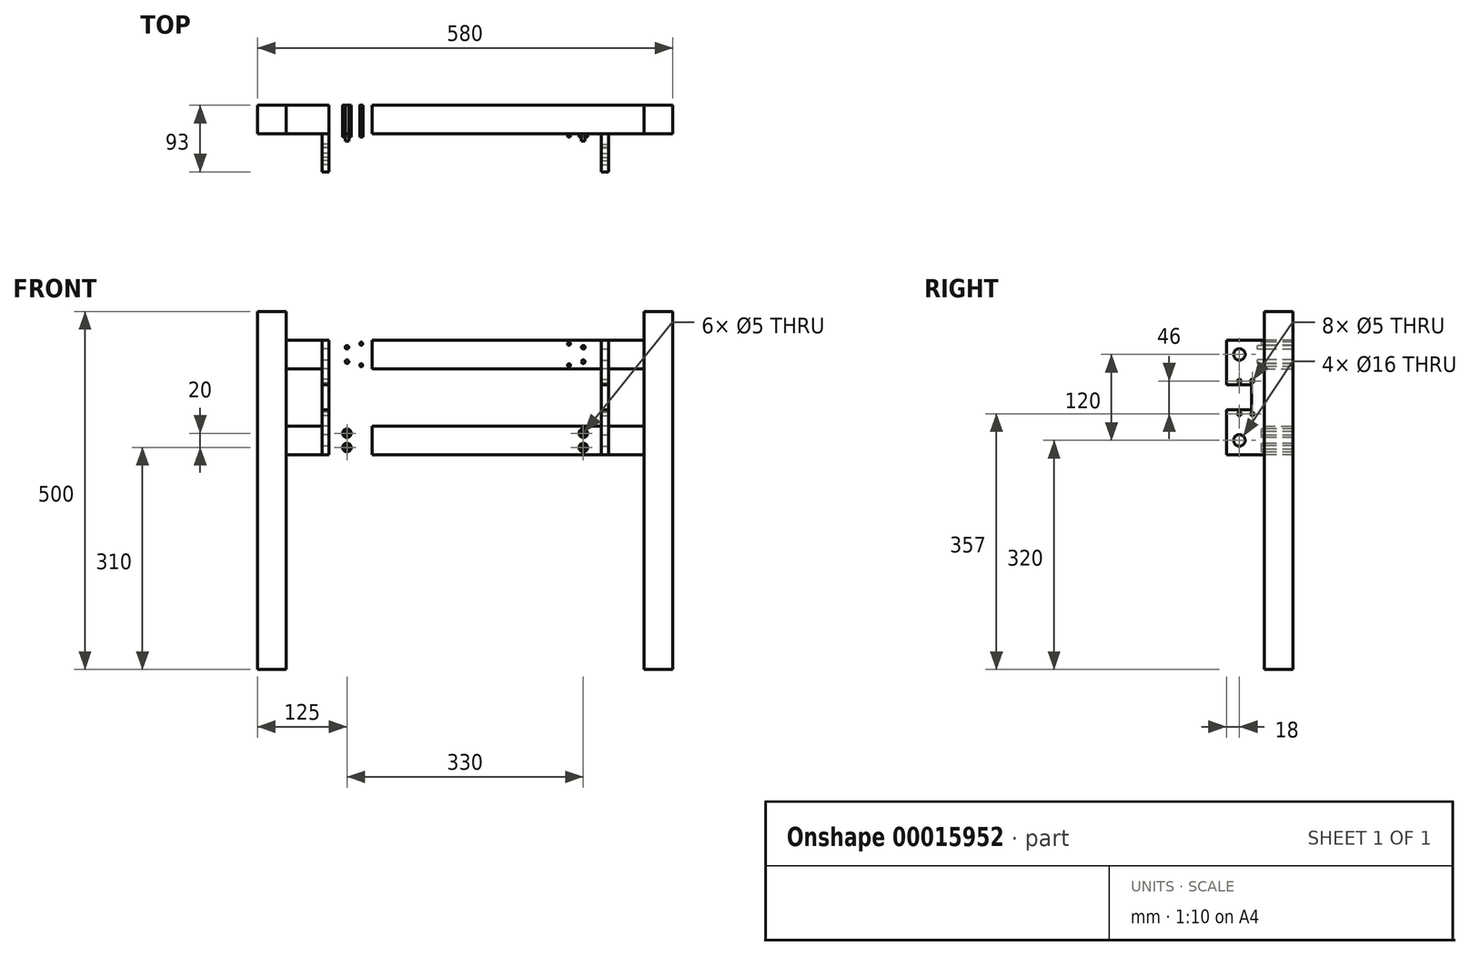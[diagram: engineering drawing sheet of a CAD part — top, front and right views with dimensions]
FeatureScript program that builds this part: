
annotation { "Feature Type Name" : "Feature", "Feature Type Description" : "" }
export const myFeature = defineFeature(function(context is Context, id is Id, definition is map)
    precondition{}
    {
        {
            var Q0;
            Q0=qCreatedBy(makeId("Top.planeOp"),FACE);
            var sketch = newSketch(context, id + "F0", { "sketchPlane" : qUnion([Q0])});
            skLineSegment(sketch, "E0.bottom", {"start": v(0, 0) * mm, "end": v(40, 0) * mm});
            skLineSegment(sketch, "E0.top", {"start": v(0, 40) * mm, "end": v(40, 40) * mm});
            skLineSegment(sketch, "E0.left", {"start": v(0, 0) * mm, "end": v(0, 40) * mm});
            skLineSegment(sketch, "E0.right", {"start": v(40, 0) * mm, "end": v(40, 40) * mm});
            skSolve(sketch);
        }
        {
            var Q0;
            Q0 = qSketchRegion(id + "F0", true);
            extrude(context, id + "F1", {"entities" : qUnion([Q0]), "depth" : 500 * mm});
        }
        {
            var Q0;
            Q0=makeQuery(id+"F1.opExtrude","SWEPT_FACE",FACE,{"disambiguationData":[OSD([sQuery(id+"F0.wireOp",EDGE,"E0.right")])]});
            cPlane(context, id + "F2", {"entities" : qUnion([Q0]), "cplaneType" : CPlaneType.OFFSET, "offset" : 250 * mm, "width" : 150 * mm, "height" : 150 * mm});
        }
        {
            var Q0;
            Q0=makeQuery(id+"F1.opExtrude","SWEPT_BODY",BODY,{"disambiguationData":[OSD([sQuery(id+"F0.wireOp",EDGE,"E0.bottom"),sQuery(id+"F0.wireOp",EDGE,"E0.top"),sQuery(id+"F0.wireOp",EDGE,"E0.left"),sQuery(id+"F0.wireOp",EDGE,"E0.right")])]});
            var Q1;
            Q1=qCreatedBy(id+"F2.planeOp",FACE);
            mirror(context, id + "F3", {"entities" : qUnion([Q0]), "mirrorPlane" : qUnion([Q1])});
        }
        {
            var Q0;
            Q0=makeQuery(id+"F1.opExtrude","SWEPT_FACE",FACE,{"disambiguationData":[OSD([sQuery(id+"F0.wireOp",EDGE,"E0.right")])]});
            var sketch = newSketch(context, id + "F4", { "sketchPlane" : qUnion([Q0])});
            skLineSegment(sketch, "E1.0", {"start": v(0, 460) * mm, "end": v(40, 460) * mm, "construction": true});
            skLineSegment(sketch, "E2.0", {"start": v(0, 420) * mm, "end": v(40, 420) * mm, "construction": true});
            skLineSegment(sketch, "E3.0", {"start": v(0, 440) * mm, "end": v(40, 440) * mm, "construction": true});
            skLineSegment(sketch, "E4.0", {"start": v(0, 380) * mm, "end": v(40, 380) * mm, "construction": true});
            skLineSegment(sketch, "E5.0", {"start": v(0, 320) * mm, "end": v(40, 320) * mm, "construction": true});
            skLineSegment(sketch, "E6.0", {"start": v(0, 300) * mm, "end": v(40, 300) * mm, "construction": true});
            skLineSegment(sketch, "E7.0", {"start": v(0, 340) * mm, "end": v(40, 340) * mm, "construction": true});
            skLineSegment(sketch, "E8.bottom", {"start": v(0, 460) * mm, "end": v(40, 460) * mm});
            skLineSegment(sketch, "E8.top", {"start": v(0, 420) * mm, "end": v(40, 420) * mm});
            skLineSegment(sketch, "E8.left", {"start": v(0, 460) * mm, "end": v(0, 420) * mm});
            skLineSegment(sketch, "E8.right", {"start": v(40, 460) * mm, "end": v(40, 420) * mm});
            skLineSegment(sketch, "E9.bottom", {"start": v(0, 340) * mm, "end": v(40, 340) * mm});
            skLineSegment(sketch, "E9.top", {"start": v(0, 300) * mm, "end": v(40, 300) * mm});
            skLineSegment(sketch, "E9.left", {"start": v(0, 340) * mm, "end": v(0, 300) * mm});
            skLineSegment(sketch, "E9.right", {"start": v(40, 340) * mm, "end": v(40, 300) * mm});
            skSolve(sketch);
        }
        {
            var Q0;
            Q0 = qSketchRegion(id + "F4", true);
            extrude(context, id + "F5", {"entities" : qUnion([Q0]), "depth" : 500 * mm});
        }
        {
            var Q0;
            Q0=makeQuery(id+"F5.opExtrude","CAP_FACE",FACE,{"disambiguationData":[OSD([sQuery(id+"F4.wireOp",EDGE,"E8.bottom"),sQuery(id+"F4.wireOp",EDGE,"E8.top"),sQuery(id+"F4.wireOp",EDGE,"E8.left"),sQuery(id+"F4.wireOp",EDGE,"E8.right")])],"isStart":true});
            cPlane(context, id + "F6", {"entities" : qUnion([Q0]), "cplaneType" : CPlaneType.OFFSET, "offset" : 250 * mm, "oppositeDirection" : true, "width" : 150 * mm, "height" : 150 * mm});
        }
        {
            var Q0;
            Q0=qCreatedBy(id+"F6.planeOp",FACE);
            cPlane(context, id + "F7", {"entities" : qUnion([Q0]), "cplaneType" : CPlaneType.OFFSET, "offset" : 200 * mm, "width" : 150 * mm, "height" : 150 * mm});
        }
        {
            var Q0;
            Q0=makeQuery(id+"F5.opExtrude","CAP_FACE",FACE,{"disambiguationData":[OSD([sQuery(id+"F4.wireOp",EDGE,"E8.bottom"),sQuery(id+"F4.wireOp",EDGE,"E8.top"),sQuery(id+"F4.wireOp",EDGE,"E8.left"),sQuery(id+"F4.wireOp",EDGE,"E8.right")])],"isStart":true});
            var sketch = newSketch(context, id + "F8", { "sketchPlane" : qUnion([Q0])});
            skLineSegment(sketch, "E10.0", {"start": v(10, 460) * mm, "end": v(10, 420) * mm, "construction": true});
            skSolve(sketch);
        }
        {
            var Q0;
            Q0=qCreatedBy(id+"F7.planeOp",FACE);
            var sketch = newSketch(context, id + "F9", { "sketchPlane" : qUnion([Q0])});
            skLineSegment(sketch, "E11.0", {"start": v(10, 460) * mm, "end": v(10, 420) * mm, "construction": true});
            skLineSegment(sketch, "E12.0", {"start": v(0, 460) * mm, "end": v(0, 420) * mm, "construction": true});
            skLineSegment(sketch, "E13.0", {"start": v(35, 460) * mm, "end": v(35, 420) * mm, "construction": true});
            skLineSegment(sketch, "E14", {"start": v(35, 440) * mm, "end": v(10, 440) * mm, "construction": true});
            skCircle(sketch, "E15", {"center": v(35, 440) * mm, "radius": 8 * mm});
            skLineSegment(sketch, "E16.0", {"start": v(35, 380) * mm, "end": v(10, 380) * mm, "construction": true});
            skCircle(sketch, "E17", {"center": v(35, 380) * mm, "radius": 8 * mm});
            skCircle(sketch, "E18.MirrorC", {"center": v(35, 320) * mm, "radius": 8 * mm});
            skLineSegment(sketch, "E19", {"start": v(35, 440) * mm, "end": v(35, 380) * mm, "construction": true});
            skLineSegment(sketch, "E20.0", {"start": v(10, 440) * mm, "end": v(10, 380) * mm, "construction": true});
            skLineSegment(sketch, "E21.0", {"start": v(0, 440) * mm, "end": v(0, 380) * mm, "construction": true});
            skLineSegment(sketch, "E22.0", {"start": v(35, 403) * mm, "end": v(10, 403) * mm, "construction": true});
            skLineSegment(sketch, "E23.0", {"start": v(17, 440) * mm, "end": v(17, 380) * mm, "construction": true});
            skCircle(sketch, "E24", {"center": v(35, 403) * mm, "radius": 2.5 * mm});
            skCircle(sketch, "E25", {"center": v(17, 403) * mm, "radius": 2.5 * mm});
            skLineSegment(sketch, "E26.0", {"start": v(53, 460) * mm, "end": v(53, 420) * mm, "construction": true});
            skLineSegment(sketch, "E27.0", {"start": v(35, 300) * mm, "end": v(10, 300) * mm, "construction": true});
            skLineSegment(sketch, "E28.bottom", {"start": v(0, 460) * mm, "end": v(53, 460) * mm});
            skLineSegment(sketch, "E28.top", {"start": v(0, 300) * mm, "end": v(53, 300) * mm});
            skLineSegment(sketch, "E28.left", {"start": v(0, 460) * mm, "end": v(0, 300) * mm});
            skLineSegment(sketch, "E28.right", {"start": v(53, 460) * mm, "end": v(53, 300) * mm});
            skCircle(sketch, "E29.MirrorC", {"center": v(17, 357) * mm, "radius": 2.5 * mm});
            skCircle(sketch, "E30.MirrorC", {"center": v(35, 357) * mm, "radius": 2.5 * mm});
            skSolve(sketch);
        }
        {
            var Q0;
            Q0 = qSketchRegion(id + "F9", true);
            extrude(context, id + "F10", {"entities" : qUnion([Q0]), "oppositeDirection" : true, "depth" : 10 * mm});
        }
        {
            var Q0;
            Q0=makeQuery(id+"F5.opExtrude","SWEPT_FACE",FACE,{"disambiguationData":[OSD([sQuery(id+"F4.wireOp",EDGE,"E9.left")])]});
            var sketch = newSketch(context, id + "F11", { "sketchPlane" : qUnion([Q0])});
            skLineSegment(sketch, "E31.bottom", {"start": v(100, 300) * mm, "end": v(160, 300) * mm});
            skLineSegment(sketch, "E31.top", {"start": v(100, 460) * mm, "end": v(160, 460) * mm});
            skLineSegment(sketch, "E31.left", {"start": v(100, 300) * mm, "end": v(100, 460) * mm});
            skLineSegment(sketch, "E31.right", {"start": v(160, 300) * mm, "end": v(160, 460) * mm});
            skSolve(sketch);
        }
        {
            var Q0;
            Q0 = qSketchRegion(id + "F11", true);
            extrude(context, id + "F12", {"entities" : qUnion([Q0]), "depth" : 10 * mm});
        }
        {
            var Q0;
            Q0=makeQuery(id+"F12.opExtrude","CAP_FACE",FACE,{"disambiguationData":[OSD([sQuery(id+"F11.wireOp",EDGE,"E31.bottom"),sQuery(id+"F11.wireOp",EDGE,"E31.top"),sQuery(id+"F11.wireOp",EDGE,"E31.left"),sQuery(id+"F11.wireOp",EDGE,"E31.right")])],"isStart":false});
            var sketch = newSketch(context, id + "F13", { "sketchPlane" : qUnion([Q0])});
            skLineSegment(sketch, "E32.0", {"start": v(160, 320) * mm, "end": v(100, 320) * mm, "construction": true});
            skLineSegment(sketch, "E33.0", {"start": v(160, 305) * mm, "end": v(100, 305) * mm, "construction": true});
            skLineSegment(sketch, "E34.0", {"start": v(160, 335) * mm, "end": v(100, 335) * mm, "construction": true});
            skLineSegment(sketch, "E35.0", {"start": v(95, 460) * mm, "end": v(95, 300) * mm, "construction": true});
            skLineSegment(sketch, "E36.0", {"start": v(145, 460) * mm, "end": v(145, 300) * mm, "construction": true});
            skCircle(sketch, "E37", {"center": v(145, 335) * mm, "radius": 2.1 * mm});
            skCircle(sketch, "E38", {"center": v(145, 305) * mm, "radius": 2.1 * mm});
            skLineSegment(sketch, "E39.0", {"start": v(160, 330) * mm, "end": v(100, 330) * mm, "construction": true});
            skLineSegment(sketch, "E40.0", {"start": v(160, 310) * mm, "end": v(100, 310) * mm, "construction": true});
            skLineSegment(sketch, "E41.0", {"start": v(125, 460) * mm, "end": v(125, 300) * mm, "construction": true});
            skCircle(sketch, "E42", {"center": v(125, 330) * mm, "radius": 2.5 * mm});
            skCircle(sketch, "E43", {"center": v(125, 310) * mm, "radius": 2.5 * mm});
            skCircle(sketch, "E44", {"center": v(125, 330) * mm, "radius": 6 * mm});
            skCircle(sketch, "E45", {"center": v(125, 310) * mm, "radius": 6 * mm});
            skLineSegment(sketch, "E46.0", {"start": v(100, 380) * mm, "end": v(160, 380) * mm, "construction": true});
            skCircle(sketch, "E47.MirrorC", {"center": v(125, 430) * mm, "radius": 6 * mm});
            skCircle(sketch, "E48.MirrorC", {"center": v(125, 430) * mm, "radius": 2.5 * mm});
            skCircle(sketch, "E49.MirrorC", {"center": v(125, 450) * mm, "radius": 6 * mm});
            skCircle(sketch, "E50.MirrorC", {"center": v(125, 450) * mm, "radius": 2.5 * mm});
            skCircle(sketch, "E51.MirrorC", {"center": v(145, 425) * mm, "radius": 2.1 * mm});
            skCircle(sketch, "E52.MirrorC", {"center": v(145, 455) * mm, "radius": 2.1 * mm});
            skSolve(sketch);
        }
        {
            var Q0;
            Q0=makeQuery(id+"F13.imprint","IMPRINT",FACE,{"disambiguationData":[TD([[makeQuery(id+"F13.imprint","IMPRINT",EDGE,{"derivedFrom":sQuery(id+"F13.wireOp",EDGE,"E37")}),1.0]])]});
            var Q1;
            Q1=makeQuery(id+"F13.imprint","IMPRINT",FACE,{"disambiguationData":[TD([[makeQuery(id+"F13.imprint","IMPRINT",EDGE,{"derivedFrom":sQuery(id+"F13.wireOp",EDGE,"E38")}),1.0]])]});
            var Q2;
            Q2=makeQuery(id+"F13.imprint","IMPRINT",FACE,{"disambiguationData":[TD([[makeQuery(id+"F13.imprint","IMPRINT",EDGE,{"derivedFrom":sQuery(id+"F13.wireOp",EDGE,"E51.MirrorC")}),-1.0]])]});
            var Q3;
            Q3=makeQuery(id+"F13.imprint","IMPRINT",FACE,{"disambiguationData":[TD([[makeQuery(id+"F13.imprint","IMPRINT",EDGE,{"derivedFrom":sQuery(id+"F13.wireOp",EDGE,"E52.MirrorC")}),-1.0]])]});
            var Q4;
            Q4=makeQuery(id+"F13.imprint","IMPRINT",FACE,{"disambiguationData":[TD([[makeQuery(id+"F13.imprint","IMPRINT",EDGE,{"derivedFrom":sQuery(id+"F13.wireOp",EDGE,"E42")}),1.0]])]});
            var Q5;
            Q5=makeQuery(id+"F13.imprint","IMPRINT",FACE,{"disambiguationData":[TD([[makeQuery(id+"F13.imprint","IMPRINT",EDGE,{"derivedFrom":sQuery(id+"F13.wireOp",EDGE,"E43")}),1.0]])]});
            var Q6;
            Q6=makeQuery(id+"F13.imprint","IMPRINT",FACE,{"disambiguationData":[TD([[makeQuery(id+"F13.imprint","IMPRINT",EDGE,{"derivedFrom":sQuery(id+"F13.wireOp",EDGE,"E50.MirrorC")}),-1.0]])]});
            var Q7;
            Q7=makeQuery(id+"F13.imprint","IMPRINT",FACE,{"disambiguationData":[TD([[makeQuery(id+"F13.imprint","IMPRINT",EDGE,{"derivedFrom":sQuery(id+"F13.wireOp",EDGE,"E48.MirrorC")}),-1.0]])]});
            extrude(context, id + "F14", {"entities" : qUnion([Q0, Q1, Q2, Q3, Q4, Q5, Q6, Q7]), "operationType" : NewBodyOperationType.REMOVE, "endBound" : BoundingType.THROUGH_ALL, "oppositeDirection" : true, "depth" : 25 * mm});
        }
        {
            var Q0;
            Q0 = qSketchRegion(id + "F13", true);
            extrude(context, id + "F15", {"entities" : qUnion([Q0]), "operationType" : NewBodyOperationType.REMOVE, "oppositeDirection" : true, "depth" : 6 * mm});
        }
        {
            var Q0;
            Q0=makeQuery(id+"F10.opExtrude","SWEPT_BODY",BODY,{"disambiguationData":[OSD([sQuery(id+"F9.wireOp",EDGE,"E15"),sQuery(id+"F9.wireOp",EDGE,"E17"),sQuery(id+"F9.wireOp",EDGE,"E18.MirrorC"),sQuery(id+"F9.wireOp",EDGE,"E24"),sQuery(id+"F9.wireOp",EDGE,"E25"),sQuery(id+"F9.wireOp",EDGE,"E28.bottom"),sQuery(id+"F9.wireOp",EDGE,"E28.top"),sQuery(id+"F9.wireOp",EDGE,"E28.left"),sQuery(id+"F9.wireOp",EDGE,"E28.right"),sQuery(id+"F9.wireOp",EDGE,"E29.MirrorC"),sQuery(id+"F9.wireOp",EDGE,"E30.MirrorC")])]});
            var Q1;
            Q1=makeQuery(id+"F12.opExtrude","SWEPT_BODY",BODY,{"disambiguationData":[OSD([sQuery(id+"F11.wireOp",EDGE,"E31.bottom"),sQuery(id+"F11.wireOp",EDGE,"E31.top"),sQuery(id+"F11.wireOp",EDGE,"E31.left"),sQuery(id+"F11.wireOp",EDGE,"E31.right")])]});
            var Q2;
            Q2=qCreatedBy(id+"F6.planeOp",FACE);
            mirror(context, id + "F16", {"entities" : qUnion([Q0, Q1]), "mirrorPlane" : qUnion([Q2])});
        }
        {
            var Q0;
            Q0=makeQuery(id+"F16.opPattern","COPY",FACE,{"derivedFrom":makeQuery(id+"F10.opExtrude","CAP_FACE",FACE,{"disambiguationData":[OSD([sQuery(id+"F9.wireOp",EDGE,"E15"),sQuery(id+"F9.wireOp",EDGE,"E17"),sQuery(id+"F9.wireOp",EDGE,"E18.MirrorC"),sQuery(id+"F9.wireOp",EDGE,"E24"),sQuery(id+"F9.wireOp",EDGE,"E25"),sQuery(id+"F9.wireOp",EDGE,"E28.bottom"),sQuery(id+"F9.wireOp",EDGE,"E28.top"),sQuery(id+"F9.wireOp",EDGE,"E28.left"),sQuery(id+"F9.wireOp",EDGE,"E28.right"),sQuery(id+"F9.wireOp",EDGE,"E29.MirrorC"),sQuery(id+"F9.wireOp",EDGE,"E30.MirrorC")])],"isStart":true}),"instanceName":"1"});
            var sketch = newSketch(context, id + "F17", { "sketchPlane" : qUnion([Q0])});
            skLineSegment(sketch, "E53.0", {"start": v(-18, 457.36) * mm, "end": v(-18, 302.64) * mm, "construction": true});
            skLineSegment(sketch, "E54", {"start": v(-18, 380) * mm, "end": v(-53, 380) * mm, "construction": true});
            skLineSegment(sketch, "E55.rect.bottom", {"start": v(-18, 397.5) * mm, "end": v(-53, 397.5) * mm});
            skLineSegment(sketch, "E55.rect.top", {"start": v(-18, 362.5) * mm, "end": v(-53, 362.5) * mm});
            skLineSegment(sketch, "E55.rect.left", {"start": v(-18, 397.5) * mm, "end": v(-18, 362.5) * mm});
            skLineSegment(sketch, "E55.rect.right", {"start": v(-53, 397.5) * mm, "end": v(-53, 362.5) * mm});
            skPoint(sketch, "E55.rect.middle", {"position": v(-35.5, 380) * mm});
            skSolve(sketch);
        }
        {
            var Q0;
            Q0 = qSketchRegion(id + "F17", true);
            extrude(context, id + "F18", {"entities" : qUnion([Q0]), "operationType" : NewBodyOperationType.REMOVE, "endBound" : BoundingType.THROUGH_ALL, "oppositeDirection" : true, "depth" : 25 * mm});
        }
    });
